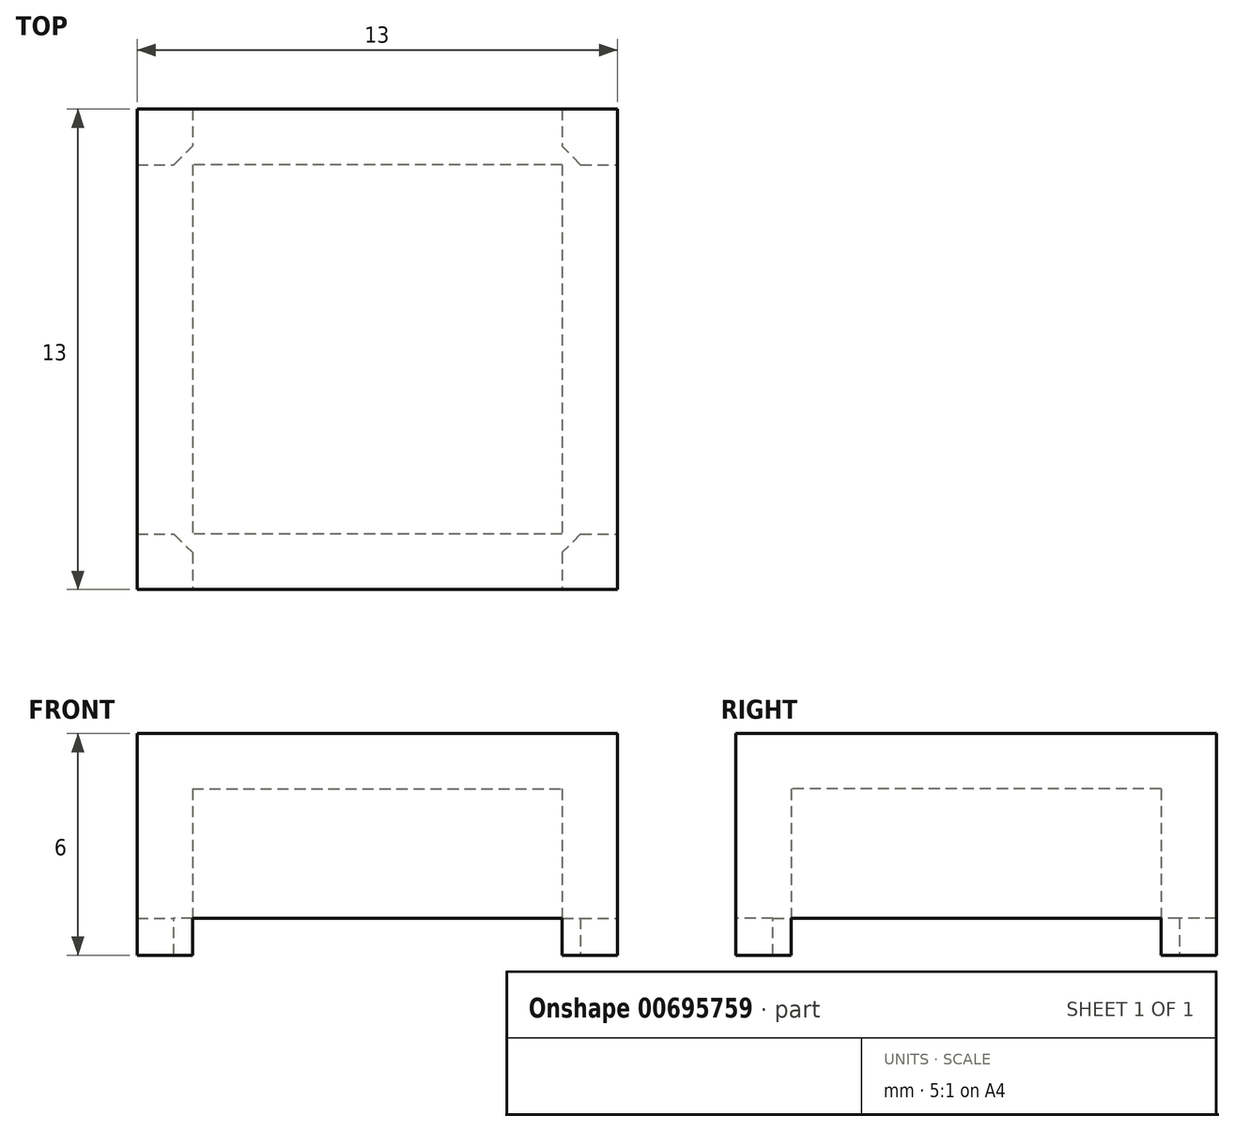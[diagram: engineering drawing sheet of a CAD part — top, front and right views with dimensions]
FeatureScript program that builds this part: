
annotation { "Feature Type Name" : "Feature", "Feature Type Description" : "" }
export const myFeature = defineFeature(function(context is Context, id is Id, definition is map)
    precondition{}
    {
        {
            var Q0;
            Q0=qCreatedBy(makeId("Top.planeOp"),FACE);
            var sketch = newSketch(context, id + "F0", { "sketchPlane" : qUnion([Q0])});
            skLineSegment(sketch, "E0.bottom", {"start": v(-6.5, 6.5) * mm, "end": v(6.5, 6.5) * mm});
            skLineSegment(sketch, "E0.top", {"start": v(-6.5, -6.5) * mm, "end": v(6.5, -6.5) * mm});
            skLineSegment(sketch, "E0.left", {"start": v(-6.5, 6.5) * mm, "end": v(-6.5, -6.5) * mm});
            skLineSegment(sketch, "E0.right", {"start": v(6.5, 6.5) * mm, "end": v(6.5, -6.5) * mm});
            skPoint(sketch, "E0.middle", {"position": v(0, 0) * mm});
            skSolve(sketch);
        }
        {
            var Q0;
            Q0=makeQuery(id+"F0.imprint","IMPRINT",FACE,{"disambiguationData":[TD([[makeQuery(id+"F0.imprint","IMPRINT",EDGE,{"derivedFrom":sQuery(id+"F0.wireOp",EDGE,"E0.bottom")}),-1.0]])]});
            extrude(context, id + "F1", {"entities" : qUnion([Q0]), "depth" : 6 * mm, "offsetDistance" : 25 * mm});
        }
        {
            var Q0;
            Q0=qCreatedBy(makeId("Top.planeOp"),FACE);
            var sketch = newSketch(context, id + "F2", { "sketchPlane" : qUnion([Q0])});
            skLineSegment(sketch, "E1.bottom", {"start": v(-5, 5) * mm, "end": v(5, 5) * mm});
            skLineSegment(sketch, "E1.top", {"start": v(-5, -5) * mm, "end": v(5, -5) * mm});
            skLineSegment(sketch, "E1.left", {"start": v(-5, 5) * mm, "end": v(-5, -5) * mm});
            skLineSegment(sketch, "E1.right", {"start": v(5, 5) * mm, "end": v(5, -5) * mm});
            skPoint(sketch, "E1.middle", {"position": v(0, 0) * mm});
            skSolve(sketch);
        }
        {
            var Q0;
            Q0 = qSketchRegion(id + "F2", true);
            extrude(context, id + "F3", {"entities" : qUnion([Q0]), "operationType" : NewBodyOperationType.REMOVE, "depth" : 4.5 * mm, "offsetDistance" : 25 * mm});
        }
        {
            var Q0;
            Q0=qCreatedBy(makeId("Right.planeOp"),FACE);
            var sketch = newSketch(context, id + "F4", { "sketchPlane" : qUnion([Q0])});
            skLineSegment(sketch, "E2.bottom", {"start": v(5, 1) * mm, "end": v(-5, 1) * mm});
            skLineSegment(sketch, "E2.top", {"start": v(5, -1) * mm, "end": v(-5, -1) * mm});
            skLineSegment(sketch, "E2.left", {"start": v(5, 1) * mm, "end": v(5, -1) * mm});
            skLineSegment(sketch, "E2.right", {"start": v(-5, 1) * mm, "end": v(-5, -1) * mm});
            skPoint(sketch, "E2.middle", {"position": v(0, 0) * mm});
            skSolve(sketch);
        }
        {
            var Q0;
            Q0=makeQuery(id+"F4.imprint","IMPRINT",FACE,{"disambiguationData":[TD([[makeQuery(id+"F4.imprint","IMPRINT",EDGE,{"derivedFrom":sQuery(id+"F4.wireOp",EDGE,"E2.bottom")}),1.0]])]});
            extrude(context, id + "F5", {"entities" : qUnion([Q0]), "operationType" : NewBodyOperationType.REMOVE, "endBound" : BoundingType.SYMMETRIC, "oppositeDirection" : true, "depth" : 25 * mm, "offsetDistance" : 25 * mm});
        }
        {
            var Q0;
            Q0=qCreatedBy(makeId("Front.planeOp"),FACE);
            var sketch = newSketch(context, id + "F6", { "sketchPlane" : qUnion([Q0])});
            skLineSegment(sketch, "E3.bottom", {"start": v(-5, 1) * mm, "end": v(5, 1) * mm});
            skLineSegment(sketch, "E3.top", {"start": v(-5, -1) * mm, "end": v(5, -1) * mm});
            skLineSegment(sketch, "E3.left", {"start": v(-5, 1) * mm, "end": v(-5, -1) * mm});
            skLineSegment(sketch, "E3.right", {"start": v(5, 1) * mm, "end": v(5, -1) * mm});
            skPoint(sketch, "E3.middle", {"position": v(0, 0) * mm});
            skSolve(sketch);
        }
        {
            var Q0;
            Q0 = qSketchRegion(id + "F6", true);
            extrude(context, id + "F7", {"entities" : qUnion([Q0]), "operationType" : NewBodyOperationType.REMOVE, "endBound" : BoundingType.SYMMETRIC, "oppositeDirection" : true, "depth" : 25 * mm, "offsetDistance" : 25 * mm});
        }
        {
            var Q0;
            Q0=makeQuery(id+"F7.boolean.opBoolean","INTERSECT",EDGE,{"derivedFrom":[makeQuery(id+"F5.boolean.opBoolean","MERGE",FACE,{"derivedFrom":[makeQuery(id+"F3.boolean.opBoolean","COPY",FACE,{"derivedFrom":makeQuery(id+"F3.opExtrude","SWEPT_FACE",FACE,{"disambiguationData":[OSD([sQuery(id+"F2.wireOp",EDGE,"E1.top")])]})}),makeQuery(id+"F5.opExtrude","SWEPT_FACE",FACE,{"disambiguationData":[OSD([sQuery(id+"F4.wireOp",EDGE,"E2.right")])]})]}),makeQuery(id+"F7.opExtrude","SWEPT_FACE",FACE,{"disambiguationData":[OSD([sQuery(id+"F6.wireOp",EDGE,"E3.right")])]})]});
            var Q1;
            Q1=makeQuery(id+"F7.boolean.opBoolean","INTERSECT",EDGE,{"derivedFrom":[makeQuery(id+"F5.boolean.opBoolean","MERGE",FACE,{"derivedFrom":[makeQuery(id+"F3.boolean.opBoolean","COPY",FACE,{"derivedFrom":makeQuery(id+"F3.opExtrude","SWEPT_FACE",FACE,{"disambiguationData":[OSD([sQuery(id+"F2.wireOp",EDGE,"E1.bottom")])]})}),makeQuery(id+"F5.opExtrude","SWEPT_FACE",FACE,{"disambiguationData":[OSD([sQuery(id+"F4.wireOp",EDGE,"E2.left")])]})]}),makeQuery(id+"F7.opExtrude","SWEPT_FACE",FACE,{"disambiguationData":[OSD([sQuery(id+"F6.wireOp",EDGE,"E3.right")])]})]});
            var Q2;
            Q2=makeQuery(id+"F7.boolean.opBoolean","INTERSECT",EDGE,{"derivedFrom":[makeQuery(id+"F5.boolean.opBoolean","MERGE",FACE,{"derivedFrom":[makeQuery(id+"F3.boolean.opBoolean","COPY",FACE,{"derivedFrom":makeQuery(id+"F3.opExtrude","SWEPT_FACE",FACE,{"disambiguationData":[OSD([sQuery(id+"F2.wireOp",EDGE,"E1.top")])]})}),makeQuery(id+"F5.opExtrude","SWEPT_FACE",FACE,{"disambiguationData":[OSD([sQuery(id+"F4.wireOp",EDGE,"E2.right")])]})]}),makeQuery(id+"F7.opExtrude","SWEPT_FACE",FACE,{"disambiguationData":[OSD([sQuery(id+"F6.wireOp",EDGE,"E3.left")])]})]});
            var Q3;
            Q3=makeQuery(id+"F7.boolean.opBoolean","INTERSECT",EDGE,{"derivedFrom":[makeQuery(id+"F5.boolean.opBoolean","MERGE",FACE,{"derivedFrom":[makeQuery(id+"F3.boolean.opBoolean","COPY",FACE,{"derivedFrom":makeQuery(id+"F3.opExtrude","SWEPT_FACE",FACE,{"disambiguationData":[OSD([sQuery(id+"F2.wireOp",EDGE,"E1.bottom")])]})}),makeQuery(id+"F5.opExtrude","SWEPT_FACE",FACE,{"disambiguationData":[OSD([sQuery(id+"F4.wireOp",EDGE,"E2.left")])]})]}),makeQuery(id+"F7.opExtrude","SWEPT_FACE",FACE,{"disambiguationData":[OSD([sQuery(id+"F6.wireOp",EDGE,"E3.left")])]})]});
            chamfer(context, id + "F8", {"entities" : qUnion([Q0, Q1, Q2, Q3]), "width" : 0.5 * mm, "tangentPropagation" : true});
        }
    });
